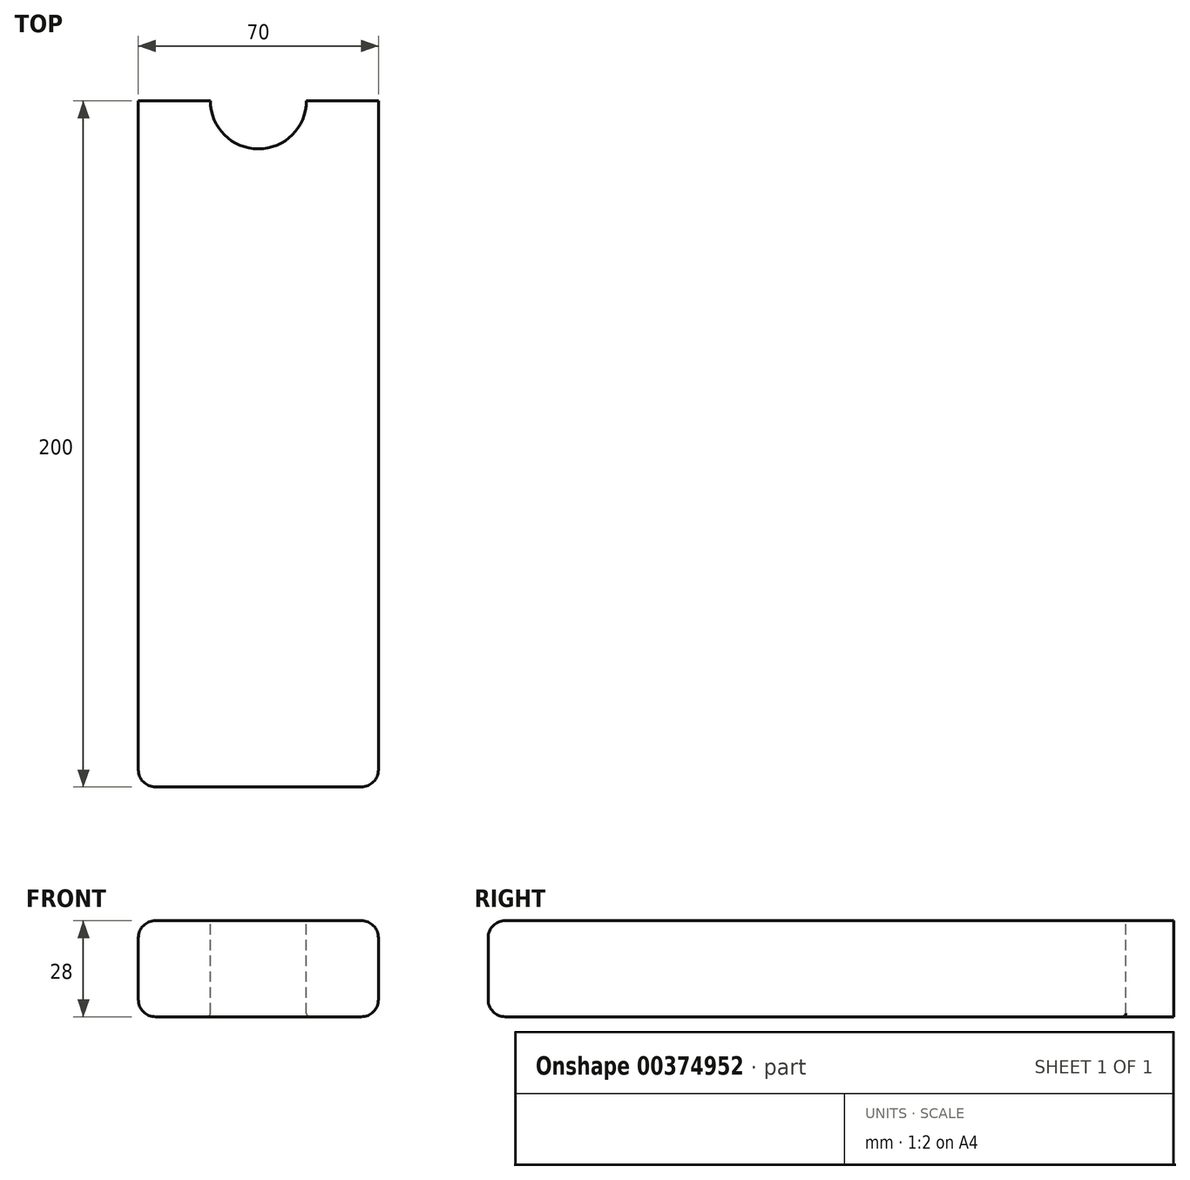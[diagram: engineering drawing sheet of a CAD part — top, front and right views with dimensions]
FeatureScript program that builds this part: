
annotation { "Feature Type Name" : "Feature", "Feature Type Description" : "" }
export const myFeature = defineFeature(function(context is Context, id is Id, definition is map)
    precondition{}
    {
        {
            var Q0;
            Q0=qCreatedBy(makeId("Front.planeOp"),FACE);
            var sketch = newSketch(context, id + "F0", { "sketchPlane" : qUnion([Q0])});
            skLineSegment(sketch, "E0.bottom", {"start": v(35, -14) * mm, "end": v(-35, -14) * mm});
            skLineSegment(sketch, "E0.top", {"start": v(35, 14) * mm, "end": v(-35, 14) * mm});
            skLineSegment(sketch, "E0.left", {"start": v(35, -14) * mm, "end": v(35, 14) * mm});
            skLineSegment(sketch, "E0.right", {"start": v(-35, -14) * mm, "end": v(-35, 14) * mm});
            skPoint(sketch, "E0.middle", {"position": v(0, 0) * mm});
            skSolve(sketch);
        }
        {
            var Q0;
            Q0 = qSketchRegion(id + "F0", true);
            extrude(context, id + "F1", {"entities" : qUnion([Q0]), "depth" : 200 * mm});
        }
        {
            var Q0;
            Q0=makeQuery(id+"F1.opExtrude","SWEPT_FACE",FACE,{"disambiguationData":[OSD([sQuery(id+"F0.wireOp",EDGE,"E0.top")])]});
            var sketch = newSketch(context, id + "F2", { "sketchPlane" : qUnion([Q0])});
            skCircle(sketch, "E1", {"center": v(0, 0) * mm, "radius": 14 * mm});
            skSolve(sketch);
        }
        {
            var Q0;
            Q0 = qSketchRegion(id + "F2", true);
            extrude(context, id + "F3", {"entities" : qUnion([Q0]), "operationType" : NewBodyOperationType.REMOVE, "endBound" : BoundingType.THROUGH_ALL, "oppositeDirection" : true, "depth" : 25 * mm});
        }
        {
            var Q0;
            Q0=makeQuery(id+"F1.opExtrude","SWEPT_EDGE",EDGE,{"disambiguationData":[OSD([sQuery(id+"F0.wireOp",EDGE,"E0.top"),sQuery(id+"F0.wireOp",EDGE,"E0.right")])]});
            var Q1;
            Q1=makeQuery(id+"F1.opExtrude","SWEPT_EDGE",EDGE,{"disambiguationData":[OSD([sQuery(id+"F0.wireOp",EDGE,"E0.top"),sQuery(id+"F0.wireOp",EDGE,"E0.left")])]});
            var Q2;
            Q2=makeQuery(id+"F1.opExtrude","SWEPT_EDGE",EDGE,{"disambiguationData":[OSD([sQuery(id+"F0.wireOp",EDGE,"E0.bottom"),sQuery(id+"F0.wireOp",EDGE,"E0.left")])]});
            var Q3;
            Q3=makeQuery(id+"F1.opExtrude","SWEPT_EDGE",EDGE,{"disambiguationData":[OSD([sQuery(id+"F0.wireOp",EDGE,"E0.bottom"),sQuery(id+"F0.wireOp",EDGE,"E0.right")])]});
            var Q4;
            Q4=makeQuery(id+"F1.opExtrude","CAP_EDGE",EDGE,{"disambiguationData":[OSD([sQuery(id+"F0.wireOp",EDGE,"E0.top")])],"isStart":false});
            var Q5;
            Q5=makeQuery(id+"F1.opExtrude","CAP_EDGE",EDGE,{"disambiguationData":[OSD([sQuery(id+"F0.wireOp",EDGE,"E0.bottom")])],"isStart":false});
            var Q6;
            Q6=makeQuery(id+"F1.opExtrude","CAP_EDGE",EDGE,{"disambiguationData":[OSD([sQuery(id+"F0.wireOp",EDGE,"E0.left")])],"isStart":false});
            var Q7;
            Q7=makeQuery(id+"F1.opExtrude","CAP_EDGE",EDGE,{"disambiguationData":[OSD([sQuery(id+"F0.wireOp",EDGE,"E0.right")])],"isStart":false});
            fillet(context, id + "F4", {"entities" : qUnion([Q0, Q1, Q2, Q3, Q4, Q5, Q6, Q7]), "radius" : 5 * mm, "tangentPropagation" : true, "allowEdgeOverflow" : false});
        }
        {
            var Q0;
            Q0=makeQuery(id+"F3.boolean.opBoolean","INTERSECT",EDGE,{"derivedFrom":[makeQuery(id+"F1.opExtrude","SWEPT_FACE",FACE,{"disambiguationData":[OSD([sQuery(id+"F0.wireOp",EDGE,"E0.bottom")])]}),makeQuery(id+"F3.opExtrude","SWEPT_FACE",FACE,{"disambiguationData":[OSD([sQuery(id+"F2.wireOp",EDGE,"E1")])]})]});
            var Q1;
            Q1=makeQuery(id+"F3.boolean.opBoolean","COPY",EDGE,{"derivedFrom":makeQuery(id+"F3.opExtrude","CAP_EDGE",EDGE,{"disambiguationData":[OSD([sQuery(id+"F2.wireOp",EDGE,"E1")])],"isStart":true})});
            fillet(context, id + "F5", {"entities" : qUnion([Q0, Q1]), "radius" : 1 * mm, "tangentPropagation" : true, "allowEdgeOverflow" : false});
        }
    });
